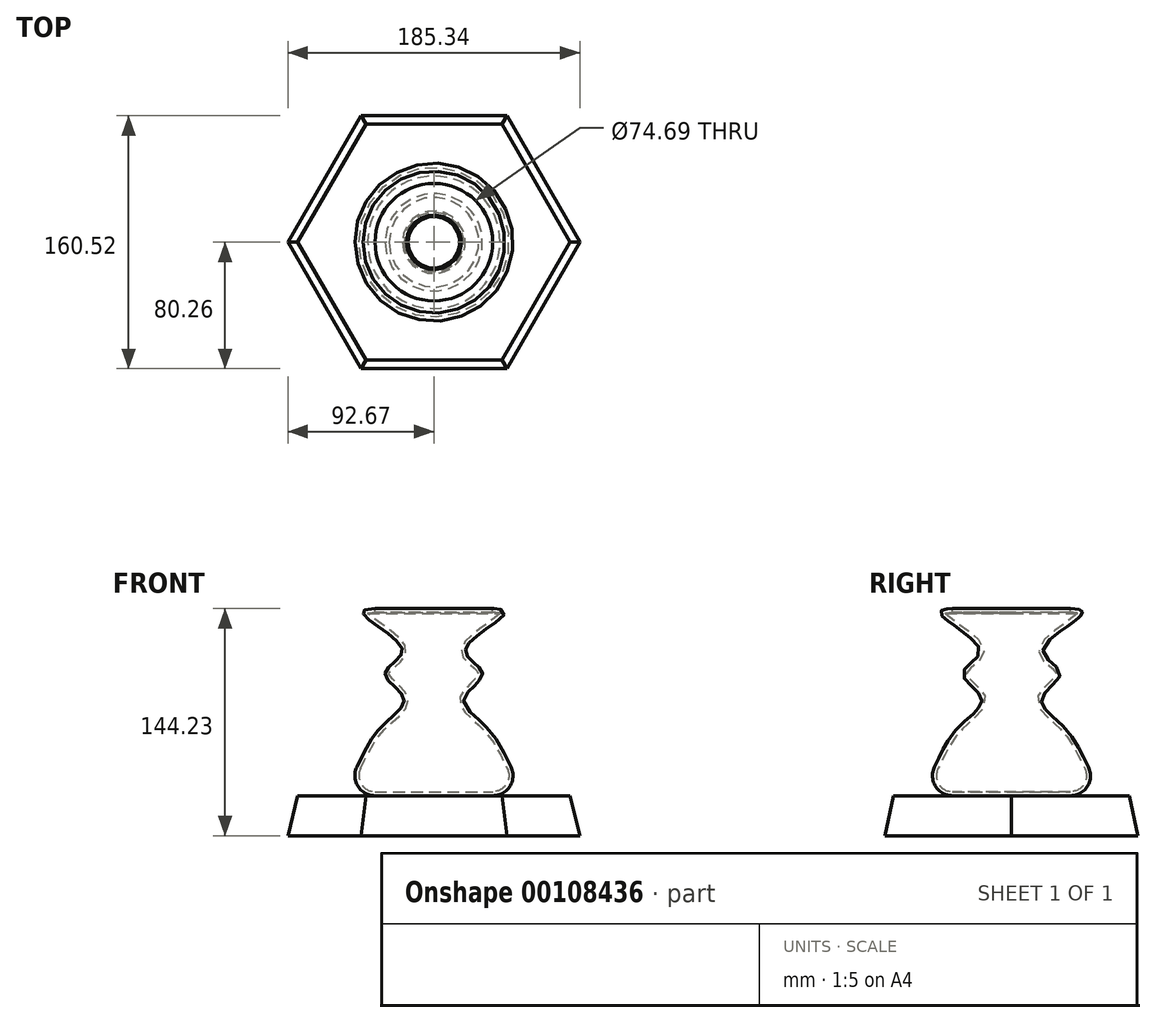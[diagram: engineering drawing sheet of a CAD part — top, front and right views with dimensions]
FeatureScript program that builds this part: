
annotation { "Feature Type Name" : "Feature", "Feature Type Description" : "" }
export const myFeature = defineFeature(function(context is Context, id is Id, definition is map)
    precondition{}
    {
        {
            var Q0;
            Q0=qCreatedBy(makeId("Front.planeOp"),FACE);
            var sketch = newSketch(context, id + "F0", { "sketchPlane" : qUnion([Q0])});
            skLineSegment(sketch, "E0", {"start": v(0, 0) * mm, "end": v(0, 101.4) * mm, "construction": true});
            skLineSegment(sketch, "E1", {"start": v(0, 0) * mm, "end": v(-37.44, 0) * mm});
            skArc(sketch, "E2", {"start": v(-37.44, 0) * mm, "mid": v(-48.26, 6.03) * mm, "end": v(-48.84, 18.4) * mm});
            skFitSpline(sketch, "E3", {"points": [v(-48.84, 18.4) * mm, v(-33.2, 43.84) * mm, v(-19.03, 61.71) * mm, v(-31, 77.64) * mm, v(-20.02, 91.15) * mm, v(-40.2, 110.9) * mm, v(-1.28, 114.61) * mm], "startDerivative": vector(74.67, 150.14) * mm, "endDerivative": vector(716.74, -117.73) * mm});
            skLineSegment(sketch, "E4", {"start": v(-37.35, 118.83) * mm, "end": v(0, 118.83) * mm});
            skLineSegment(sketch, "E5", {"start": v(0, 118.83) * mm, "end": v(0, 0) * mm});
            skSolve(sketch);
        }
        {
            var Q0;
            Q0=makeQuery(id+"F0.imprint","IMPRINT",FACE,{"disambiguationData":[TD([[makeQuery(id+"F0.imprint","IMPRINT",EDGE,{"derivedFrom":sQuery(id+"F0.wireOp",EDGE,"E1")}),-1.0]])]});
            var Q1;
            Q1=sQuery(id+"F0.wireOp",EDGE,"E3");
            var Q2;
            Q2=sQuery(id+"F0.wireOp",EDGE,"E2");
            var Q3;
            Q3=sQuery(id+"F0.wireOp",EDGE,"E1");
            var Q4;
            Q4=sQuery(id+"F0.wireOp",EDGE,"E0");
            revolve(context, id + "F1", {"entities" : qUnion([Q0]), "surfaceEntities" : qUnion([Q1, Q2, Q3]), "axis" : qUnion([Q4]), "revolveType" : RevolveType.FULL});
        }
        {
            var Q0;
            Q0=makeQuery(id+"F1.opRevolve","SWEPT_FACE",FACE,{"disambiguationData":[OSD([sQuery(id+"F0.wireOp",EDGE,"E4")])]});
            shell(context, id + "F2", {"entities" : qUnion([Q0]), "thickness" : 2.54 * mm});
        }
        {
            var Q0;
            Q0=qCreatedBy(makeId("Top.planeOp"),FACE);
            var sketch = newSketch(context, id + "F3", { "sketchPlane" : qUnion([Q0])});
            skCircle(sketch, "E6.cCircle", {"center": v(0, 0) * mm, "radius": 74.86 * mm, "construction": true});
            skLineSegment(sketch, "E6.0", {"start": v(-43.22, 74.86) * mm, "end": v(43.22, 74.86) * mm});
            skLineSegment(sketch, "E6.1", {"start": v(43.22, 74.86) * mm, "end": v(86.44, 0) * mm});
            skLineSegment(sketch, "E6.2", {"start": v(86.44, 0) * mm, "end": v(43.22, -74.86) * mm});
            skLineSegment(sketch, "E6.3", {"start": v(43.22, -74.86) * mm, "end": v(-43.22, -74.86) * mm});
            skLineSegment(sketch, "E6.4", {"start": v(-43.22, -74.86) * mm, "end": v(-86.44, 0) * mm});
            skLineSegment(sketch, "E6.5", {"start": v(-86.44, 0) * mm, "end": v(-43.22, 74.86) * mm});
            skPoint(sketch, "E6.0.midPoint", {"position": v(0, 74.86) * mm});
            skSolve(sketch);
        }
        {
            var Q0;
            Q0=makeQuery(id+"F3.imprint","IMPRINT",FACE,{"disambiguationData":[TD([[makeQuery(id+"F3.imprint","IMPRINT",EDGE,{"derivedFrom":sQuery(id+"F3.wireOp",EDGE,"E6.0")}),-1.0]])]});
            extrude(context, id + "F4", {"entities" : qUnion([Q0]), "oppositeDirection" : true, "depth" : 25.4 * mm, "hasDraft" : true, "draftAngle" : 12 * degree});
        }
    });
